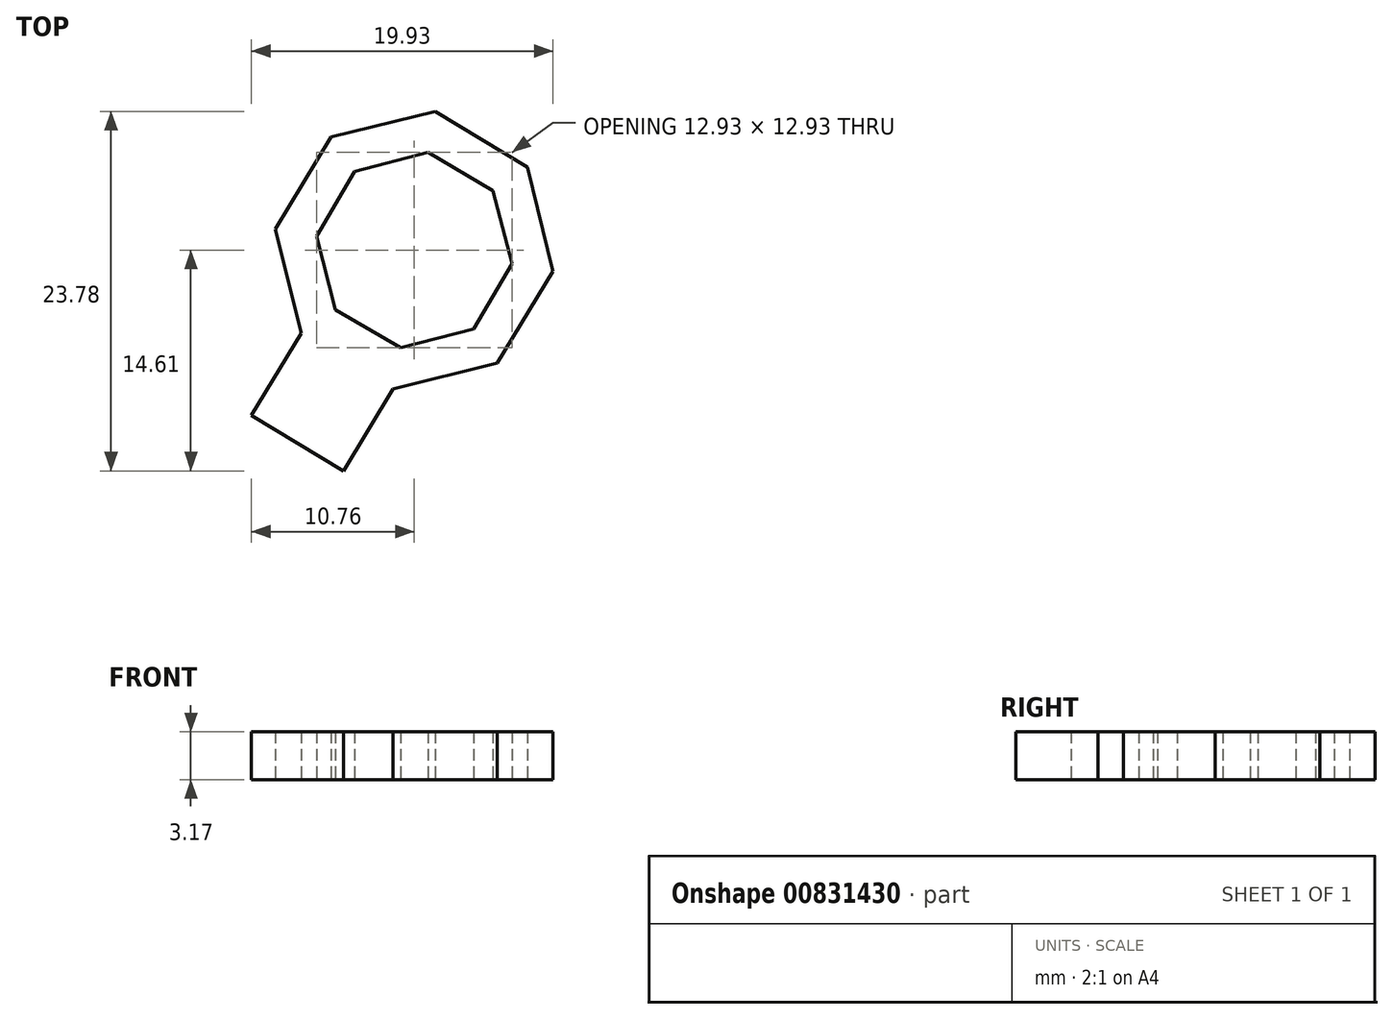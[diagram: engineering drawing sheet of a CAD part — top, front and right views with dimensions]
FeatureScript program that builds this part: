
annotation { "Feature Type Name" : "Feature", "Feature Type Description" : "" }
export const myFeature = defineFeature(function(context is Context, id is Id, definition is map)
    precondition{}
    {
        {
            var Q0;
            Q0=qCreatedBy(makeId("Top.planeOp"),FACE);
            var sketch = newSketch(context, id + "F0", { "sketchPlane" : qUnion([Q0])});
            skCircle(sketch, "E0.cCircle", {"center": v(0, 0) * mm, "radius": 6.03 * mm, "construction": true});
            skLineSegment(sketch, "E0.0", {"start": v(-6.47, 0.9) * mm, "end": v(-3.93, 5.21) * mm});
            skLineSegment(sketch, "E0.1", {"start": v(-3.93, 5.21) * mm, "end": v(0.9, 6.47) * mm});
            skLineSegment(sketch, "E0.2", {"start": v(0.9, 6.47) * mm, "end": v(5.21, 3.93) * mm});
            skLineSegment(sketch, "E0.3", {"start": v(5.21, 3.93) * mm, "end": v(6.47, -0.9) * mm});
            skLineSegment(sketch, "E0.4", {"start": v(6.47, -0.9) * mm, "end": v(3.93, -5.21) * mm});
            skLineSegment(sketch, "E0.5", {"start": v(3.93, -5.21) * mm, "end": v(-0.9, -6.47) * mm});
            skLineSegment(sketch, "E0.6", {"start": v(-0.9, -6.47) * mm, "end": v(-5.21, -3.93) * mm});
            skLineSegment(sketch, "E0.7", {"start": v(-5.21, -3.93) * mm, "end": v(-6.47, 0.9) * mm});
            skPoint(sketch, "E0.0.midPoint", {"position": v(-5.2, 3.06) * mm});
            skCircle(sketch, "E1.cCircle", {"center": v(0, 0) * mm, "radius": 8.57 * mm, "construction": true});
            skLineSegment(sketch, "E1.0", {"start": v(-5.5, 7.48) * mm, "end": v(1.4, 9.17) * mm});
            skLineSegment(sketch, "E1.1", {"start": v(1.4, 9.17) * mm, "end": v(7.48, 5.5) * mm});
            skLineSegment(sketch, "E1.2", {"start": v(7.48, 5.5) * mm, "end": v(9.17, -1.4) * mm});
            skLineSegment(sketch, "E1.3", {"start": v(9.17, -1.4) * mm, "end": v(5.5, -7.48) * mm});
            skLineSegment(sketch, "E1.4", {"start": v(5.5, -7.48) * mm, "end": v(-1.4, -9.17) * mm});
            skLineSegment(sketch, "E1.5", {"start": v(-1.4, -9.17) * mm, "end": v(-7.48, -5.5) * mm});
            skLineSegment(sketch, "E1.6", {"start": v(-7.48, -5.5) * mm, "end": v(-9.17, 1.4) * mm});
            skLineSegment(sketch, "E1.7", {"start": v(-9.17, 1.4) * mm, "end": v(-5.5, 7.48) * mm});
            skPoint(sketch, "E1.0.midPoint", {"position": v(-2.05, 8.32) * mm});
            skLineSegment(sketch, "E2", {"start": v(-1.4, -9.17) * mm, "end": v(-4.69, -14.6) * mm});
            skLineSegment(sketch, "E3", {"start": v(-4.69, -14.6) * mm, "end": v(-13.1, -9.51) * mm});
            skLineSegment(sketch, "E4", {"start": v(-7.48, -5.5) * mm, "end": v(-10.76, -10.93) * mm});
            skSolve(sketch);
        }
        {
            var Q0;
            Q0=makeQuery(id+"F0.imprint","IMPRINT",FACE,{"disambiguationData":[TD([[makeQuery(id+"F0.imprint","IMPRINT",EDGE,{"derivedFrom":sQuery(id+"F0.wireOp",EDGE,"E0.0")}),1.0]])]});
            var Q1;
            Q1=makeQuery(id+"F0.imprint","IMPRINT",FACE,{"disambiguationData":[TD([[makeQuery(id+"F0.imprint","IMPRINT",EDGE,{"derivedFrom":sQuery(id+"F0.wireOp",EDGE,"E1.5")}),1.0]])]});
            extrude(context, id + "F1", {"entities" : qUnion([Q0, Q1]), "depth" : 3.17 * mm, "offsetDistance" : 25.4 * mm});
        }
    });
